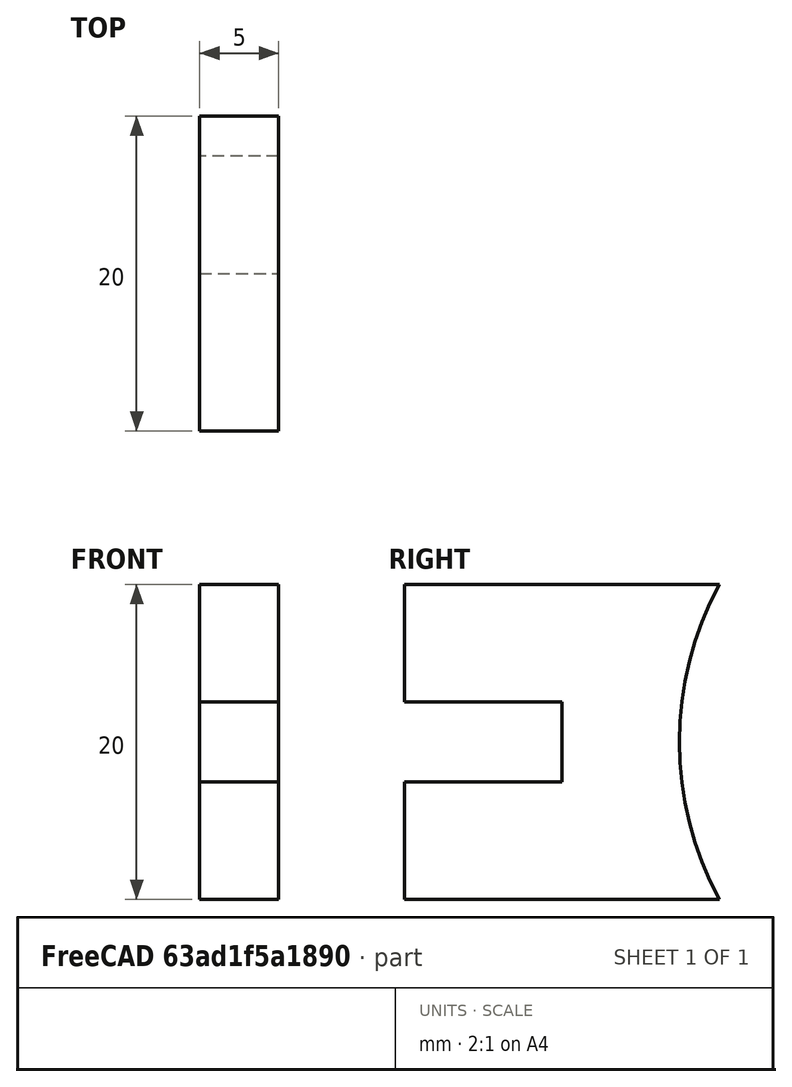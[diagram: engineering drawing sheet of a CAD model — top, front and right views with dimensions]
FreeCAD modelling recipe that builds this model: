
FCSTD DOCUMENT  (FreeCAD 1.0R39319 (Git))
Label: High Ball Holder Cross
License: All rights reserved
LicenseURL: https://en.wikipedia.org/wiki/All_rights_reserved
objects: PartDesign::CoordinateSystem×2, Sketcher::SketchObject×1, PartDesign::Pad×1, PartDesign::Body×1, App::Part×1
note: 8 computed .brp shape members not serialized (recipe doc carries the construction recipe); baked Part::Feature solids carry a one-line shape summary decoded from their .brp

FEATURE [Sketcher::SketchObject] Sketch
  ArcFitTolerance = 1e-06
  AttachmentSupport = -> [YZ_Plane001]
  FullyConstrained = true
  MakeInternals = false
  MapMode = 5
  Placement = pos=(0,0,0) rot=(0.57735,0.57735,0.57735;2.0944rad)
  sketch-geometry (9):
    g0: LineSegment StartX=10 StartY=-2.55 StartZ=0 EndX=10 EndY=2.55 EndZ=0
    g1: LineSegment StartX=10 StartY=2.55 StartZ=0 EndX=0 EndY=2.55 EndZ=0
    g2: LineSegment StartX=0 StartY=2.55 StartZ=0 EndX=0 EndY=10 EndZ=0
    g3: LineSegment StartX=0 StartY=10 StartZ=0 EndX=20 EndY=10 EndZ=0
    g4: ArcOfCircle CenterX=38.4662 CenterY=0 CenterZ=0 NormalX=0 NormalY=0 NormalZ=1 AngleXU=0 Radius=21 StartAngle=2.64528 EndAngle=3.63791
    g5: LineSegment StartX=20 StartY=-10 StartZ=0 EndX=0 EndY=-10 EndZ=0
    g6: LineSegment StartX=0 StartY=-10 StartZ=0 EndX=0 EndY=-2.55 EndZ=0
    g7: LineSegment StartX=0 StartY=-2.55 StartZ=0 EndX=10 EndY=-2.55 EndZ=0
    g8: GeomPoint [constr] X=10 Y=0 Z=0
  constraints (27):
    c: Vertical(g0)
    c: Coincident(g0,g1)
    c: Horizontal(g1)
    c: Coincident(g1,g2)
    c: Vertical(g2)
    c: Coincident(g2,g3)
    c: Horizontal(g3)
    c: Coincident(g4,g5)
    c: Coincident(g5,g6)
    c: Coincident(g6,g7)
    c: Coincident(g7,g0)
    c: Coincident(g4,g3)
    c: Horizontal(g5)
    c: Horizontal(g7)
    c: Vertical(g6)
    c: Symmetric(g0,g0,g8)
    c: Distance(g5,g3) = 20
    c: Distance(g7,g1) = 5.1
    c: Distance(g8,g3) = 10
    c: DistanceX(g3,g3) = 20
    c: PointOnObject(g1,g6)
    c: DistanceX(g7,g7) = 10
    c: Radius(g4) = 21
    c: PointOnObject(g4,g-1)
    c: PointOnObject(g8,g-1)
    c: PointOnObject(g1,g-2)
    c: Distance(g4,g-2) = 17.4662
FEATURE [PartDesign::Pad] Pad
  Direction = (1,0,0)
  Length = 5
  Length2 = 10
  Midplane = true
  Placement = pos=(0,0,0) rot=(1,1,1;2.0944rad)
  Profile = -> Sketch
  ReferenceAxis = -> Sketch [N_Axis]
  Refine = true
  Suppressed = false
  Type = 0
FEATURE [PartDesign::Body] Body  label="High Ball Holder Cross001"
  AllowCompound = false
  Group = -> [Sketch,Pad]
  Origin = -> Origin001
  Tip = -> Pad
FEATURE [PartDesign::CoordinateSystem] LCS_1
  AttacherType = Attacher::AttachEngine3D
  AttachmentOffset = pos=(0,10,0) rot=(0,0,1;0rad)
  AttachmentSupport = -> [XY_Plane001]
  MapMode = 2
  Placement = pos=(0,10,0) rot=(0,0,1;0rad)
FEATURE [PartDesign::CoordinateSystem] high_ball_ground  label="high ball ground"
  AttacherType = Attacher::AttachEngine3D
  AttachmentOffset = pos=(0,17.47,0) rot=(0,0,1;0rad)
  AttachmentSupport = -> [XY_Plane]
  MapMode = 2
  Placement = pos=(0,17.47,0) rot=(0,0,1;0rad)
FEATURE [App::Part] Part  label="High Ball Holder Cross"
  Group = -> [Body,LCS_1,high_ball_ground]
  Origin = -> Origin
